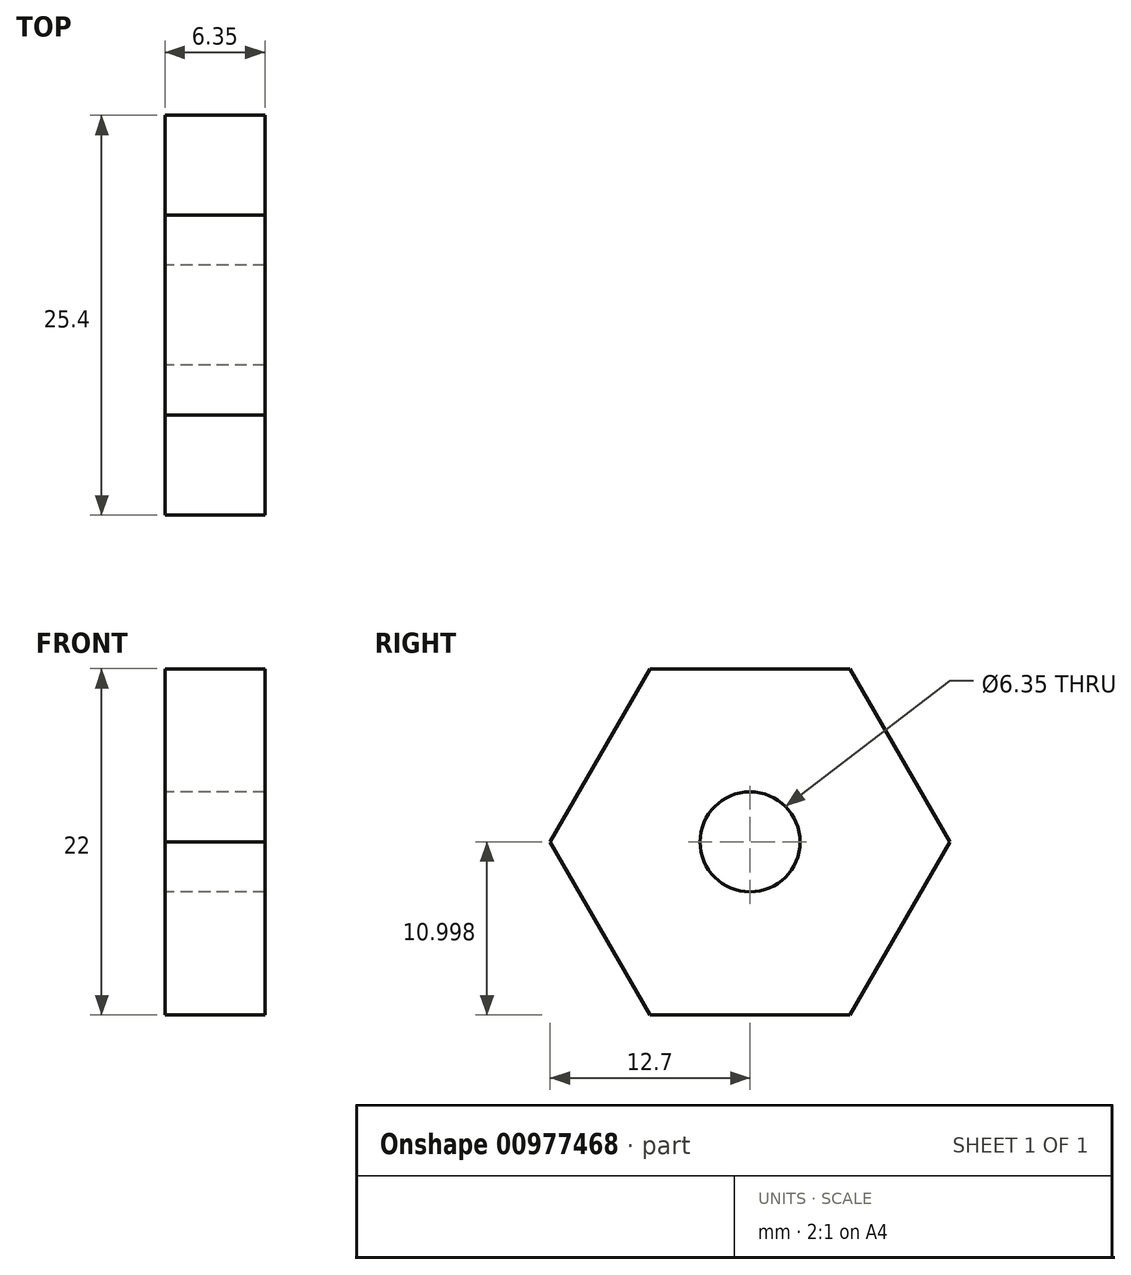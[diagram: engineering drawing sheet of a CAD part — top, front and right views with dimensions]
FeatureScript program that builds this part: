
annotation { "Feature Type Name" : "Feature", "Feature Type Description" : "" }
export const myFeature = defineFeature(function(context is Context, id is Id, definition is map)
    precondition{}
    {
        {
            var Q0;
            Q0=qCreatedBy(makeId("Right.planeOp"),FACE);
            var sketch = newSketch(context, id + "F0", { "sketchPlane" : qUnion([Q0])});
            skLineSegment(sketch, "E0", {"start": v(0, 0) * mm, "end": v(12.7, 0) * mm});
            skLineSegment(sketch, "E1", {"start": v(12.7, 0) * mm, "end": v(19.05, 11) * mm});
            skLineSegment(sketch, "E2", {"start": v(19.05, 11) * mm, "end": v(12.7, 22) * mm});
            skLineSegment(sketch, "E3", {"start": v(12.7, 22) * mm, "end": v(0, 22) * mm});
            skLineSegment(sketch, "E4", {"start": v(0, 22) * mm, "end": v(-6.35, 11) * mm});
            skLineSegment(sketch, "E5", {"start": v(-6.35, 11) * mm, "end": v(0, 0) * mm});
            skCircle(sketch, "E6", {"center": v(6.35, 11) * mm, "radius": 3.18 * mm});
            skSolve(sketch);
        }
        {
            var Q0;
            Q0 = qSketchRegion(id + "F0", true);
            extrude(context, id + "F1", {"entities" : qUnion([Q0]), "depth" : 6.35 * mm, "offsetDistance" : 25.4 * mm});
        }
    });
